FCSTD DOCUMENT  (FreeCAD 0.18R16146 (Git))
Label: plexy_glass
License: All rights reserved
LicenseURL: http://en.wikipedia.org/wiki/All_rights_reserved
objects: Sketcher::SketchObject×1, PartDesign::Body×1
note: 2 computed .brp shape members not serialized (recipe doc carries the construction recipe); baked Part::Feature solids carry a one-line shape summary decoded from their .brp

FEATURE [Sketcher::SketchObject] Sketch
  MapMode = 5
  Support = -> [XY_Plane]
  sketch-geometry (10):
    g0: LineSegment StartX=0 StartY=0 StartZ=0 EndX=500 EndY=0 EndZ=0
    g1: LineSegment StartX=500 StartY=0 StartZ=0 EndX=500 EndY=1000 EndZ=0
    g2: LineSegment [constr] StartX=500 StartY=1000 StartZ=0 EndX=0 EndY=1000 EndZ=0
    g3: LineSegment StartX=0 StartY=1000 StartZ=0 EndX=0 EndY=0 EndZ=0
    g4: LineSegment StartX=50 StartY=1000 StartZ=0 EndX=50 EndY=920 EndZ=0
    g5: LineSegment StartX=50 StartY=920 StartZ=0 EndX=450 EndY=920 EndZ=0
    g6: LineSegment StartX=450 StartY=920 StartZ=0 EndX=450 EndY=1000 EndZ=0
    g7: GeomPoint X=250 Y=1000 Z=0
    g8: LineSegment StartX=0 StartY=1000 StartZ=0 EndX=50 EndY=1000 EndZ=0
    g9: LineSegment StartX=450 StartY=1000 StartZ=0 EndX=500 EndY=1000 EndZ=0
  constraints (27):
    c: Coincident(g0,g1)
    c: Coincident(g1,g2)
    c: Coincident(g2,g3)
    c: Coincident(g3,g0)
    c: Horizontal(g0)
    c: Horizontal(g2)
    c: Vertical(g1)
    c: Vertical(g3)
    c: Coincident(g0,g-1)
    c: Distance(g0) = 500
    c: Distance(g3) = 1000
    c: Horizontal(g5)
    c: Vertical(g6)
    c: Vertical(g4)
    c: PointOnObject(g4,g2)
    c: PointOnObject(g6,g2)
    c: Coincident(g5,g6)
    c: Coincident(g4,g5)
    c: Distance(g4) = 80
    c: Distance(g5) = 400
    c: PointOnObject(g7,g2)
    c: Distance(g7,g4) = 200
    c: Distance(g7,g1) = 250
    c: Coincident(g8,g3)
    c: Coincident(g8,g4)
    c: Coincident(g9,g6)
    c: Coincident(g9,g1)
FEATURE [PartDesign::Body] Body
  Group = -> [Sketch]
  Origin = -> Origin
